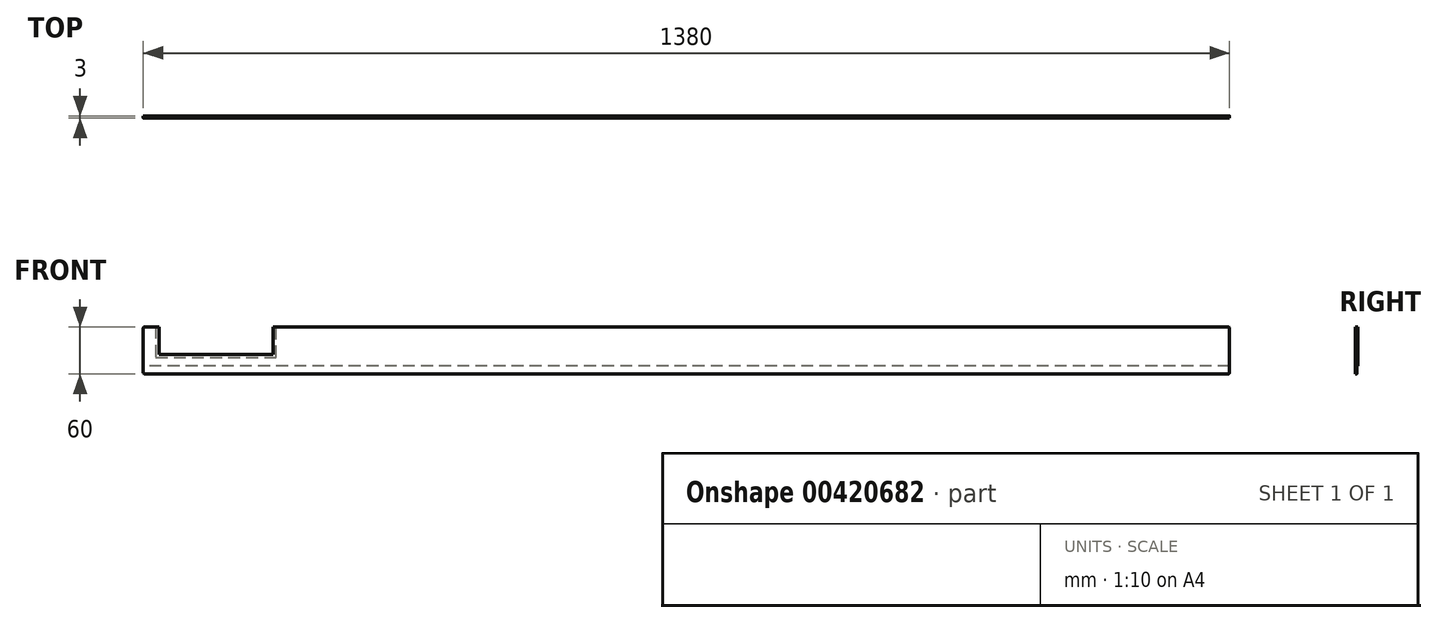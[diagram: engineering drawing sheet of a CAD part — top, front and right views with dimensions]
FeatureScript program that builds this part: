
annotation { "Feature Type Name" : "Feature", "Feature Type Description" : "" }
export const myFeature = defineFeature(function(context is Context, id is Id, definition is map)
    precondition{}
    {
        {
            var Q0;
            Q0=qCreatedBy(makeId("Front.planeOp"),FACE);
            var sketch = newSketch(context, id + "F0", { "sketchPlane" : qUnion([Q0])});
            skLineSegment(sketch, "E0.bottom", {"start": v(690, -30) * mm, "end": v(-690, -30) * mm});
            skLineSegment(sketch, "E0.top", {"start": v(690, 30) * mm, "end": v(-690, 30) * mm});
            skLineSegment(sketch, "E0.left", {"start": v(690, -30) * mm, "end": v(690, 30) * mm});
            skLineSegment(sketch, "E0.right", {"start": v(-690, -30) * mm, "end": v(-690, 30) * mm});
            skPoint(sketch, "E0.middle", {"position": v(0, 0) * mm});
            skSolve(sketch);
        }
        {
            var Q0;
            Q0=qSketchRegion(id+"F0",true);
            extrude(context, id + "F1", {"entities" : qUnion([Q0]), "depth" : 3 * mm});
        }
        {
            var Q0;
            Q0=makeQuery(id+"F1.opExtrude","CAP_FACE",FACE,{"disambiguationData":[OSD([sQuery(id+"F0.wireOp",EDGE,"E0.bottom"),sQuery(id+"F0.wireOp",EDGE,"E0.top"),sQuery(id+"F0.wireOp",EDGE,"E0.left"),sQuery(id+"F0.wireOp",EDGE,"E0.right")])],"isStart":true});
            var sketch = newSketch(context, id + "F2", { "sketchPlane" : qUnion([Q0])});
            skLineSegment(sketch, "E1", {"start": v(-690, -30) * mm, "end": v(-690, -20) * mm});
            skLineSegment(sketch, "E2", {"start": v(-690, -20) * mm, "end": v(690, -20) * mm});
            skLineSegment(sketch, "E3", {"start": v(690, -20) * mm, "end": v(690, -30) * mm});
            skLineSegment(sketch, "E4", {"start": v(690, -30) * mm, "end": v(-690, -30) * mm});
            skSolve(sketch);
        }
        {
            var Q0;
            Q0=qSketchRegion(id+"F2",true);
            extrude(context, id + "F3", {"entities" : qUnion([Q0]), "operationType" : NewBodyOperationType.REMOVE, "oppositeDirection" : true, "depth" : 1.5 * mm});
        }
        {
            var Q0;
            Q0=makeQuery(id+"F1.opExtrude","SWEPT_EDGE",EDGE,{"disambiguationData":[OSD([sQuery(id+"F0.wireOp",EDGE,"E0.bottom"),sQuery(id+"F0.wireOp",EDGE,"E0.left")])]});
            var Q1;
            Q1=makeQuery(id+"F1.opExtrude","SWEPT_EDGE",EDGE,{"disambiguationData":[OSD([sQuery(id+"F0.wireOp",EDGE,"E0.top"),sQuery(id+"F0.wireOp",EDGE,"E0.left")])]});
            var Q2;
            Q2=makeQuery(id+"F1.opExtrude","SWEPT_EDGE",EDGE,{"disambiguationData":[OSD([sQuery(id+"F0.wireOp",EDGE,"E0.top"),sQuery(id+"F0.wireOp",EDGE,"E0.right")])]});
            var Q3;
            Q3=makeQuery(id+"F1.opExtrude","SWEPT_EDGE",EDGE,{"disambiguationData":[OSD([sQuery(id+"F0.wireOp",EDGE,"E0.bottom"),sQuery(id+"F0.wireOp",EDGE,"E0.right")])]});
            fillet(context, id + "F4", {"entities" : qUnion([Q0, Q1, Q2, Q3]), "radius" : 2 * mm, "tangentPropagation" : true, "allowEdgeOverflow" : false});
        }
        {
            var Q0;
            Q0=makeQuery(id+"F1.opExtrude","CAP_FACE",FACE,{"disambiguationData":[OSD([sQuery(id+"F0.wireOp",EDGE,"E0.bottom"),sQuery(id+"F0.wireOp",EDGE,"E0.top"),sQuery(id+"F0.wireOp",EDGE,"E0.left"),sQuery(id+"F0.wireOp",EDGE,"E0.right")])],"isStart":false});
            var sketch = newSketch(context, id + "F5", { "sketchPlane" : qUnion([Q0])});
            skLineSegment(sketch, "E5", {"start": v(-670, 30) * mm, "end": v(-670, -5) * mm});
            skLineSegment(sketch, "E6", {"start": v(-670, -5) * mm, "end": v(-525, -5) * mm});
            skLineSegment(sketch, "E7", {"start": v(-525, -5) * mm, "end": v(-525, 30) * mm});
            skLineSegment(sketch, "E8", {"start": v(-525, 30) * mm, "end": v(-670, 30) * mm});
            skSolve(sketch);
        }
        {
            var Q0;
            Q0=qSketchRegion(id+"F5",true);
            extrude(context, id + "F6", {"entities" : qUnion([Q0]), "operationType" : NewBodyOperationType.REMOVE, "oppositeDirection" : true, "depth" : 3 * mm});
        }
        {
            var Q0;
            Q0=makeQuery(id+"F1.opExtrude","CAP_FACE",FACE,{"disambiguationData":[OSD([sQuery(id+"F0.wireOp",EDGE,"E0.bottom"),sQuery(id+"F0.wireOp",EDGE,"E0.top"),sQuery(id+"F0.wireOp",EDGE,"E0.left"),sQuery(id+"F0.wireOp",EDGE,"E0.right")])],"isStart":true});
            var sketch = newSketch(context, id + "F7", { "sketchPlane" : qUnion([Q0])});
            skLineSegment(sketch, "E9", {"start": v(525, 30) * mm, "end": v(525, -5) * mm});
            skLineSegment(sketch, "E10", {"start": v(525, -5) * mm, "end": v(670, -5) * mm});
            skLineSegment(sketch, "E11", {"start": v(670, -5) * mm, "end": v(670, 30) * mm});
            skLineSegment(sketch, "E12", {"start": v(670, 30) * mm, "end": v(674, 30) * mm});
            skLineSegment(sketch, "E13", {"start": v(674, 30) * mm, "end": v(674, -9) * mm});
            skLineSegment(sketch, "E14", {"start": v(674, -9) * mm, "end": v(521, -9) * mm});
            skLineSegment(sketch, "E15", {"start": v(521, -9) * mm, "end": v(521, 30) * mm});
            skLineSegment(sketch, "E16", {"start": v(521, 30) * mm, "end": v(525, 30) * mm});
            skSolve(sketch);
        }
        {
            var Q0;
            Q0=qSketchRegion(id+"F7",true);
            extrude(context, id + "F8", {"entities" : qUnion([Q0]), "operationType" : NewBodyOperationType.REMOVE, "oppositeDirection" : true, "depth" : 1.5 * mm});
        }
    });
